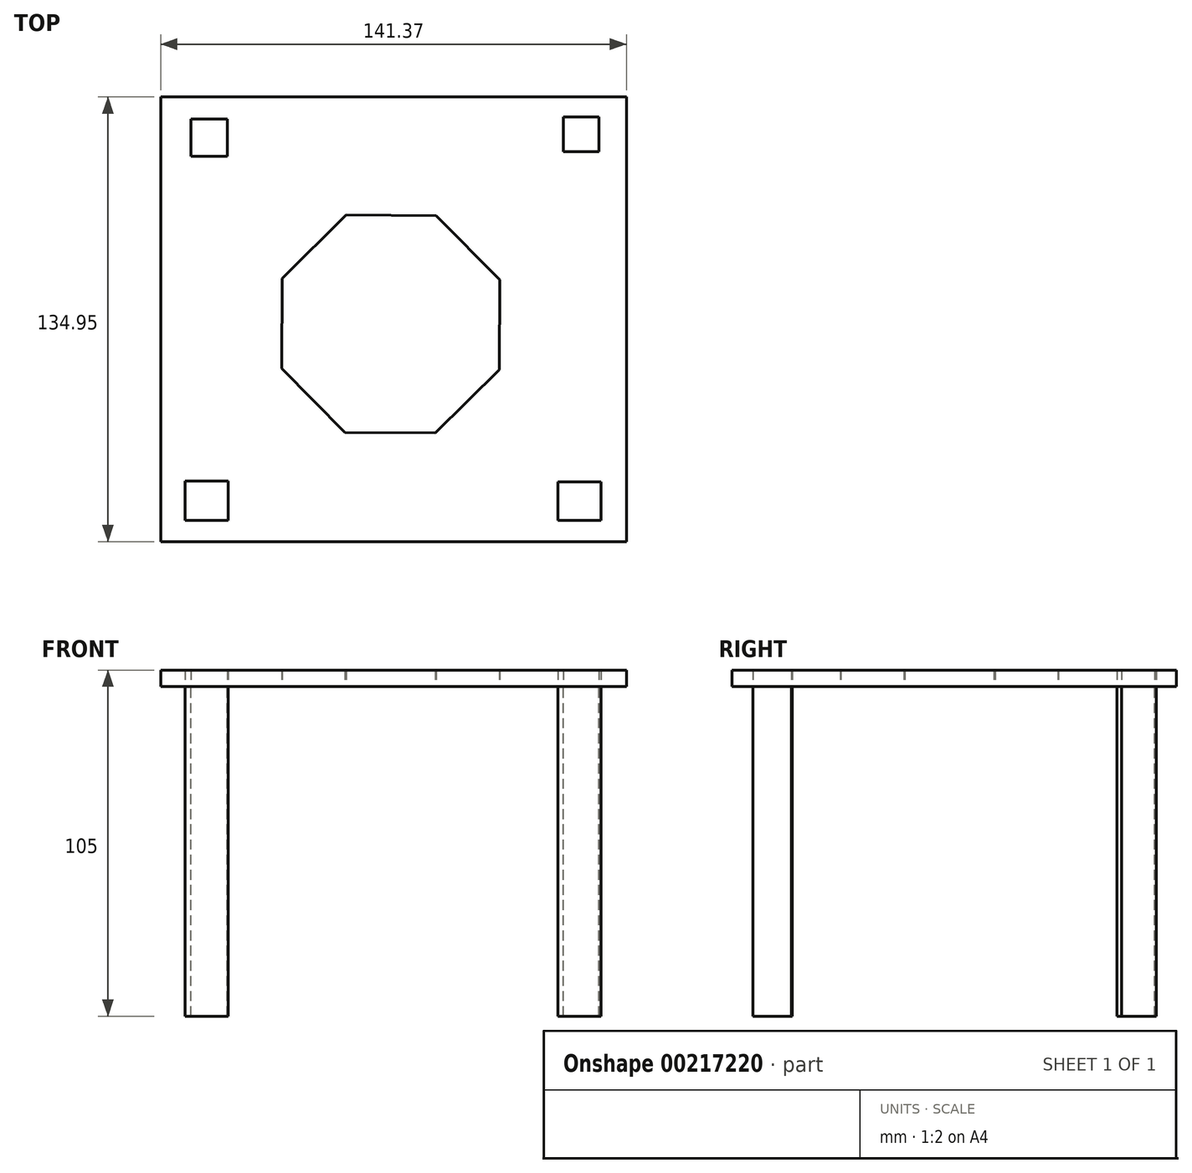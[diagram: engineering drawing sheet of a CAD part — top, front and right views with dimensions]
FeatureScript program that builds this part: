
annotation { "Feature Type Name" : "Feature", "Feature Type Description" : "" }
export const myFeature = defineFeature(function(context is Context, id is Id, definition is map)
    precondition{}
    {
        {
            var Q0;
            Q0=qCreatedBy(makeId("Top.planeOp"),FACE);
            var sketch = newSketch(context, id + "F0", { "sketchPlane" : qUnion([Q0])});
            skLineSegment(sketch, "E0.bottom", {"start": v(-69.8, 68.93) * mm, "end": v(71.56, 68.93) * mm});
            skLineSegment(sketch, "E0.top", {"start": v(-69.8, -66.02) * mm, "end": v(71.56, -66.02) * mm});
            skLineSegment(sketch, "E0.left", {"start": v(-69.8, 68.93) * mm, "end": v(-69.8, -66.02) * mm});
            skLineSegment(sketch, "E0.right", {"start": v(71.56, 68.93) * mm, "end": v(71.56, -66.02) * mm});
            skCircle(sketch, "E1.cCircle", {"center": v(0, 0) * mm, "radius": 35.73 * mm, "construction": true});
            skLineSegment(sketch, "E1.0", {"start": v(-13.5, 33.08) * mm, "end": v(13.85, 32.94) * mm});
            skLineSegment(sketch, "E1.1", {"start": v(13.85, 32.94) * mm, "end": v(33.08, 13.5) * mm});
            skLineSegment(sketch, "E1.2", {"start": v(33.08, 13.5) * mm, "end": v(32.94, -13.85) * mm});
            skLineSegment(sketch, "E1.3", {"start": v(32.94, -13.85) * mm, "end": v(13.5, -33.08) * mm});
            skLineSegment(sketch, "E1.4", {"start": v(13.5, -33.08) * mm, "end": v(-13.85, -32.94) * mm});
            skLineSegment(sketch, "E1.5", {"start": v(-13.85, -32.94) * mm, "end": v(-33.08, -13.5) * mm});
            skLineSegment(sketch, "E1.6", {"start": v(-33.08, -13.5) * mm, "end": v(-32.94, 13.85) * mm});
            skLineSegment(sketch, "E1.7", {"start": v(-32.94, 13.85) * mm, "end": v(-13.5, 33.08) * mm});
            skLineSegment(sketch, "E2.bottom", {"start": v(52.47, 62.8) * mm, "end": v(63.26, 62.8) * mm});
            skLineSegment(sketch, "E2.top", {"start": v(52.47, 52.3) * mm, "end": v(63.26, 52.3) * mm});
            skLineSegment(sketch, "E2.left", {"start": v(52.47, 62.8) * mm, "end": v(52.47, 52.3) * mm});
            skLineSegment(sketch, "E2.right", {"start": v(63.26, 62.8) * mm, "end": v(63.26, 52.3) * mm});
            skLineSegment(sketch, "E3.bottom", {"start": v(-62.38, -59.6) * mm, "end": v(-49.26, -59.6) * mm});
            skLineSegment(sketch, "E3.top", {"start": v(-62.38, -47.66) * mm, "end": v(-49.26, -47.66) * mm});
            skLineSegment(sketch, "E3.left", {"start": v(-62.38, -59.6) * mm, "end": v(-62.38, -47.66) * mm});
            skLineSegment(sketch, "E3.right", {"start": v(-49.26, -59.6) * mm, "end": v(-49.26, -47.66) * mm});
            skLineSegment(sketch, "E4.bottom", {"start": v(50.72, -59.6) * mm, "end": v(63.83, -59.6) * mm});
            skLineSegment(sketch, "E4.top", {"start": v(50.72, -47.95) * mm, "end": v(63.83, -47.95) * mm});
            skLineSegment(sketch, "E4.left", {"start": v(50.72, -59.6) * mm, "end": v(50.72, -47.95) * mm});
            skLineSegment(sketch, "E4.right", {"start": v(63.83, -59.6) * mm, "end": v(63.83, -47.95) * mm});
            skLineSegment(sketch, "E5.bottom", {"start": v(-60.63, 50.86) * mm, "end": v(-49.55, 50.86) * mm});
            skLineSegment(sketch, "E5.top", {"start": v(-60.63, 62.23) * mm, "end": v(-49.55, 62.23) * mm});
            skLineSegment(sketch, "E5.left", {"start": v(-60.63, 50.86) * mm, "end": v(-60.63, 62.23) * mm});
            skLineSegment(sketch, "E5.right", {"start": v(-49.55, 50.86) * mm, "end": v(-49.55, 62.23) * mm});
            skSolve(sketch);
        }
        {
            var Q0;
            Q0 = qSketchRegion(id + "F0", true);
            extrude(context, id + "F1", {"entities" : qUnion([Q0]), "depth" : 5 * mm});
        }
        {
            var Q0;
            Q0 = qSketchRegion(id + "F0", true);
            extrude(context, id + "F2", {"entities" : qUnion([Q0]), "operationType" : NewBodyOperationType.ADD, "depth" : 5 * mm});
        }
        {
            var Q0;
            Q0=makeQuery(id+"F0.imprint","IMPRINT",FACE,{"disambiguationData":[TD([[makeQuery(id+"F0.imprint","IMPRINT",EDGE,{"derivedFrom":sQuery(id+"F0.wireOp",EDGE,"E5.bottom")}),1.0]])]});
            var Q1;
            Q1=makeQuery(id+"F0.imprint","IMPRINT",FACE,{"disambiguationData":[TD([[makeQuery(id+"F0.imprint","IMPRINT",EDGE,{"derivedFrom":sQuery(id+"F0.wireOp",EDGE,"E3.bottom")}),1.0]])]});
            var Q2;
            Q2=makeQuery(id+"F0.imprint","IMPRINT",FACE,{"disambiguationData":[TD([[makeQuery(id+"F0.imprint","IMPRINT",EDGE,{"derivedFrom":sQuery(id+"F0.wireOp",EDGE,"E4.bottom")}),1.0]])]});
            var Q3;
            Q3=makeQuery(id+"F0.imprint","IMPRINT",FACE,{"disambiguationData":[TD([[makeQuery(id+"F0.imprint","IMPRINT",EDGE,{"derivedFrom":sQuery(id+"F0.wireOp",EDGE,"E2.bottom")}),-1.0]])]});
            extrude(context, id + "F3", {"entities" : qUnion([Q0, Q1, Q2, Q3]), "oppositeDirection" : true, "depth" : 100 * mm});
        }
    });
